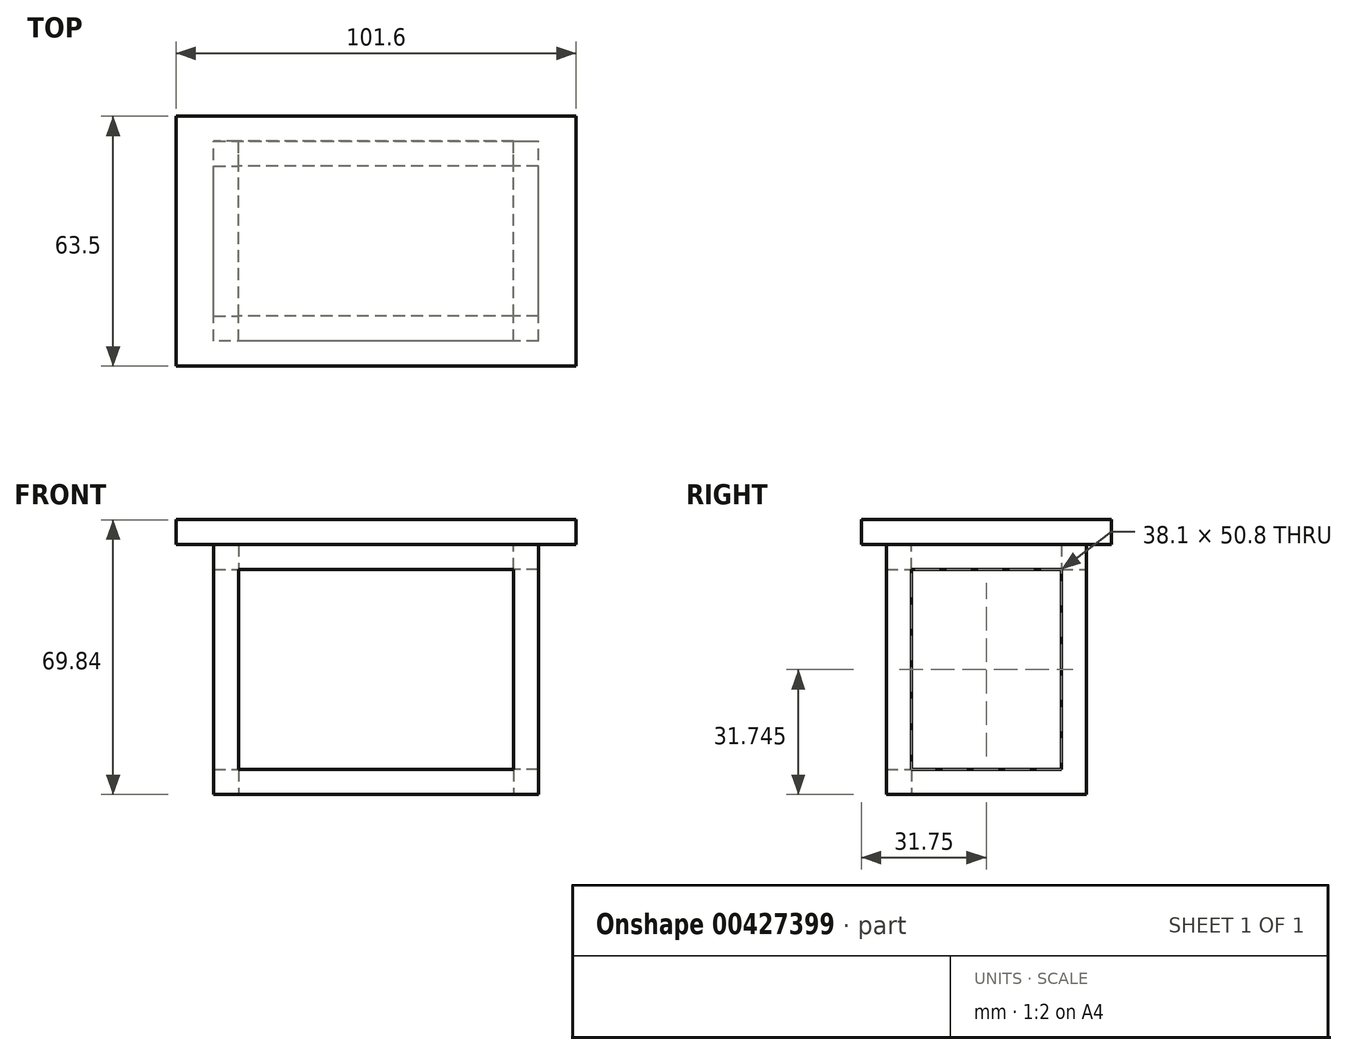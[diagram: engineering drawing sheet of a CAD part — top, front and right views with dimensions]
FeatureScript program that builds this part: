
annotation { "Feature Type Name" : "Feature", "Feature Type Description" : "" }
export const myFeature = defineFeature(function(context is Context, id is Id, definition is map)
    precondition{}
    {
        {
            var Q0;
            Q0=qCreatedBy(makeId("Front.planeOp"),FACE);
            var sketch = newSketch(context, id + "F0", { "sketchPlane" : qUnion([Q0])});
            skLineSegment(sketch, "E0", {"start": v(0, 0) * mm, "end": v(-38.1, 0) * mm});
            skLineSegment(sketch, "E1.bottom", {"start": v(-34.92, -3.17) * mm, "end": v(-41.27, -3.17) * mm});
            skLineSegment(sketch, "E1.top", {"start": v(-34.92, 3.18) * mm, "end": v(-41.27, 3.18) * mm});
            skLineSegment(sketch, "E1.left", {"start": v(-34.92, -3.17) * mm, "end": v(-34.92, 3.18) * mm});
            skLineSegment(sketch, "E1.right", {"start": v(-41.27, -3.17) * mm, "end": v(-41.27, 3.18) * mm});
            skPoint(sketch, "E1.middle", {"position": v(-38.1, 0) * mm});
            skSolve(sketch);
        }
        {
            var Q0;
            Q0 = qSketchRegion(id + "F0", true);
            extrude(context, id + "F1", {"entities" : qUnion([Q0]), "depth" : 50.8 * mm});
        }
        {
            var Q0;
            Q0=makeQuery(id+"F1.opExtrude","SWEPT_FACE",FACE,{"disambiguationData":[OSD([sQuery(id+"F0.wireOp",EDGE,"E1.top")])]});
            var sketch = newSketch(context, id + "F2", { "sketchPlane" : qUnion([Q0])});
            skLineSegment(sketch, "E2", {"start": v(-41.27, 0) * mm, "end": v(-34.92, 0) * mm});
            skLineSegment(sketch, "E3", {"start": v(-34.92, 0) * mm, "end": v(-34.92, -6.35) * mm});
            skLineSegment(sketch, "E4", {"start": v(-41.27, 0) * mm, "end": v(-41.27, -6.35) * mm});
            skLineSegment(sketch, "E5", {"start": v(-41.27, -6.35) * mm, "end": v(-34.92, -6.35) * mm});
            skLineSegment(sketch, "E6", {"start": v(-34.92, -50.8) * mm, "end": v(-41.27, -50.8) * mm});
            skLineSegment(sketch, "E7", {"start": v(-41.27, -50.8) * mm, "end": v(-41.27, -44.45) * mm});
            skLineSegment(sketch, "E8", {"start": v(-41.27, -44.45) * mm, "end": v(-41.27, -50.8) * mm});
            skLineSegment(sketch, "E9", {"start": v(-34.92, -50.8) * mm, "end": v(-34.92, -44.45) * mm});
            skLineSegment(sketch, "E10", {"start": v(-41.27, -44.45) * mm, "end": v(-34.92, -44.45) * mm});
            skSolve(sketch);
        }
        {
            var Q0;
            Q0 = qSketchRegion(id + "F2", true);
            extrude(context, id + "F3", {"entities" : qUnion([Q0]), "operationType" : NewBodyOperationType.ADD, "depth" : 50.8 * mm});
        }
        {
            var Q0;
            Q0=makeQuery(id+"F3.boolean.opBoolean","MERGE",FACE,{"derivedFrom":[makeQuery(id+"F1.opExtrude","CAP_FACE",FACE,{"disambiguationData":[OSD([sQuery(id+"F0.wireOp",EDGE,"E1.bottom"),sQuery(id+"F0.wireOp",EDGE,"E1.top"),sQuery(id+"F0.wireOp",EDGE,"E1.left"),sQuery(id+"F0.wireOp",EDGE,"E1.right")])],"isStart":false}),makeQuery(id+"F3.opExtrude","SWEPT_FACE",FACE,{"disambiguationData":[OSD([sQuery(id+"F2.wireOp",EDGE,"E6")])]})]});
            var sketch = newSketch(context, id + "F4", { "sketchPlane" : qUnion([Q0])});
            skLineSegment(sketch, "E11", {"start": v(-41.27, 53.98) * mm, "end": v(-34.92, 53.98) * mm});
            skLineSegment(sketch, "E12", {"start": v(-34.92, 53.98) * mm, "end": v(-34.92, 60.33) * mm});
            skLineSegment(sketch, "E13", {"start": v(-41.27, 53.98) * mm, "end": v(-41.27, 60.33) * mm});
            skLineSegment(sketch, "E14", {"start": v(-41.27, 60.33) * mm, "end": v(-34.92, 60.33) * mm});
            skSolve(sketch);
        }
        {
            var Q0;
            Q0 = qSketchRegion(id + "F4", true);
            extrude(context, id + "F5", {"entities" : qUnion([Q0]), "operationType" : NewBodyOperationType.ADD, "depth" : -50.8 * mm});
        }
        {
            var Q0;
            Q0=makeQuery(id+"F5.boolean.opBoolean","MERGE",FACE,{"derivedFrom":[makeQuery(id+"F3.boolean.opBoolean","MERGE",FACE,{"derivedFrom":[makeQuery(id+"F1.opExtrude","SWEPT_FACE",FACE,{"disambiguationData":[OSD([sQuery(id+"F0.wireOp",EDGE,"E1.left")])]}),makeQuery(id+"F3.opExtrude","SWEPT_FACE",FACE,{"disambiguationData":[OSD([sQuery(id+"F2.wireOp",EDGE,"E3")])]}),makeQuery(id+"F3.opExtrude","SWEPT_FACE",FACE,{"disambiguationData":[OSD([sQuery(id+"F2.wireOp",EDGE,"E9")])]})]}),makeQuery(id+"F5.opExtrude","SWEPT_FACE",FACE,{"disambiguationData":[OSD([sQuery(id+"F4.wireOp",EDGE,"E12")])]})]});
            var sketch = newSketch(context, id + "F6", { "sketchPlane" : qUnion([Q0])});
            skLineSegment(sketch, "E15", {"start": v(-44.45, 53.98) * mm, "end": v(-44.45, 60.33) * mm});
            skLineSegment(sketch, "E16", {"start": v(-44.45, 60.33) * mm, "end": v(-50.8, 60.33) * mm});
            skLineSegment(sketch, "E17", {"start": v(-50.8, 60.33) * mm, "end": v(-50.8, 53.98) * mm});
            skLineSegment(sketch, "E18", {"start": v(-50.8, 53.98) * mm, "end": v(-44.45, 53.98) * mm});
            skLineSegment(sketch, "E19", {"start": v(-6.35, 53.98) * mm, "end": v(0, 53.98) * mm});
            skLineSegment(sketch, "E20", {"start": v(0, 53.98) * mm, "end": v(0, 60.33) * mm});
            skLineSegment(sketch, "E21", {"start": v(0, 60.33) * mm, "end": v(-6.35, 60.33) * mm});
            skLineSegment(sketch, "E22", {"start": v(-6.35, 60.33) * mm, "end": v(-6.35, 53.98) * mm});
            skLineSegment(sketch, "E23", {"start": v(-44.45, 3.17) * mm, "end": v(-44.45, -3.18) * mm});
            skLineSegment(sketch, "E24", {"start": v(-44.45, -3.18) * mm, "end": v(-50.8, -3.18) * mm});
            skLineSegment(sketch, "E25", {"start": v(-50.8, -3.18) * mm, "end": v(-50.8, 3.17) * mm});
            skLineSegment(sketch, "E26", {"start": v(-50.8, 3.17) * mm, "end": v(-44.45, 3.17) * mm});
            skSolve(sketch);
        }
        {
            var Q0;
            Q0 = qSketchRegion(id + "F6", true);
            extrude(context, id + "F7", {"entities" : qUnion([Q0]), "operationType" : NewBodyOperationType.ADD, "depth" : 34.92 * mm});
        }
        {
            var Q0;
            Q0=makeQuery(id+"F1.opExtrude","SWEPT_BODY",BODY,{"disambiguationData":[OSD([sQuery(id+"F0.wireOp",EDGE,"E1.bottom"),sQuery(id+"F0.wireOp",EDGE,"E1.top"),sQuery(id+"F0.wireOp",EDGE,"E1.left"),sQuery(id+"F0.wireOp",EDGE,"E1.right")])]});
            var Q1;
            Q1=qCreatedBy(makeId("Right.planeOp"),FACE);
            mirror(context, id + "F8", {"operationType" : NewBodyOperationType.ADD, "entities" : qUnion([Q0]), "mirrorPlane" : qUnion([Q1])});
        }
        {
            var Q0;
            {var subQ0=makeQuery(id+"F7.boolean.opBoolean","MERGE",FACE,{"derivedFrom":[makeQuery(id+"F5.opExtrude","SWEPT_FACE",FACE,{"disambiguationData":[OSD([sQuery(id+"F4.wireOp",EDGE,"E14")])]}),makeQuery(id+"F7.opExtrude","SWEPT_FACE",FACE,{"disambiguationData":[OSD([sQuery(id+"F6.wireOp",EDGE,"E16")])]}),makeQuery(id+"F7.opExtrude","SWEPT_FACE",FACE,{"disambiguationData":[OSD([sQuery(id+"F6.wireOp",EDGE,"E21")])]})]});Q0=makeQuery(id+"F8.boolean.opBoolean","MERGE",FACE,{"derivedFrom":[subQ0,makeQuery(id+"F8.opPattern","COPY",FACE,{"derivedFrom":subQ0,"instanceName":"1"})]});}
            var sketch = newSketch(context, id + "F9", { "sketchPlane" : qUnion([Q0])});
            skLineSegment(sketch, "E27", {"start": v(0, 0) * mm, "end": v(0, -50.8) * mm});
            skLineSegment(sketch, "E28", {"start": v(0, -50.8) * mm, "end": v(0, -25.4) * mm});
            skLineSegment(sketch, "E29.bottom", {"start": v(50.8, -57.15) * mm, "end": v(-50.8, -57.15) * mm});
            skLineSegment(sketch, "E29.top", {"start": v(50.8, 6.35) * mm, "end": v(-50.8, 6.35) * mm});
            skLineSegment(sketch, "E29.left", {"start": v(50.8, -57.15) * mm, "end": v(50.8, 6.35) * mm});
            skLineSegment(sketch, "E29.right", {"start": v(-50.8, -57.15) * mm, "end": v(-50.8, 6.35) * mm});
            skPoint(sketch, "E29.middle", {"position": v(0, -25.4) * mm});
            skSolve(sketch);
        }
        {
            var Q0;
            Q0 = qSketchRegion(id + "F9", true);
            extrude(context, id + "F10", {"entities" : qUnion([Q0]), "operationType" : NewBodyOperationType.ADD, "depth" : 6.35 * mm});
        }
    });
